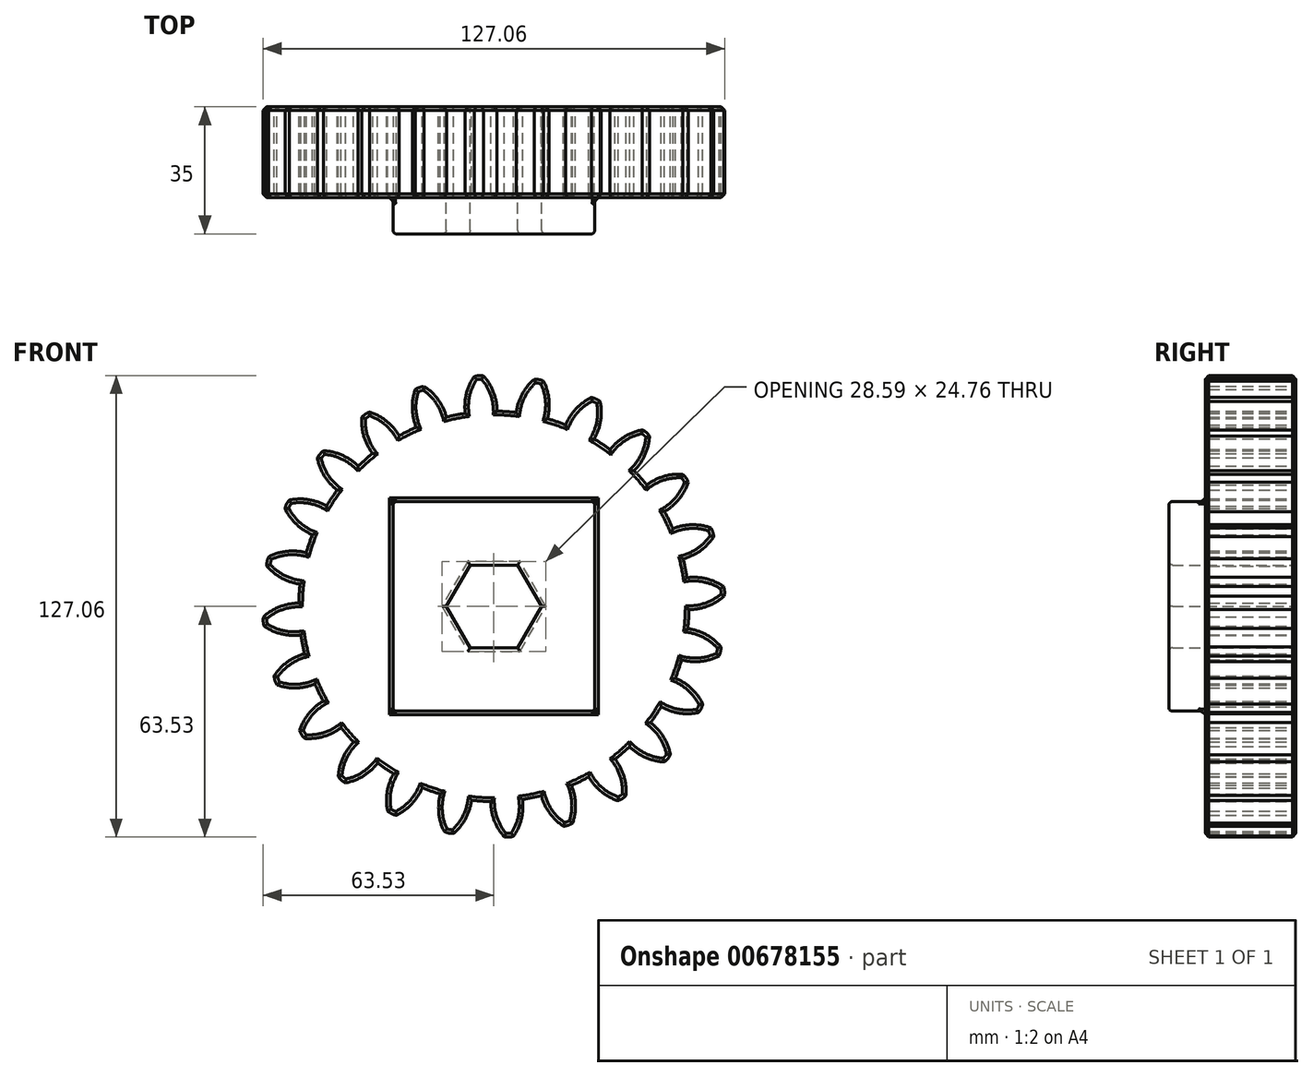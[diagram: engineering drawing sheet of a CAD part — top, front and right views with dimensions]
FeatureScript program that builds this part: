
annotation { "Feature Type Name" : "Feature", "Feature Type Description" : "" }
export const myFeature = defineFeature(function(context is Context, id is Id, definition is map)
    precondition{}
    {
        {
            var Q0;
            Q0=qCreatedBy(makeId("Front.planeOp"),FACE);
            var sketch = newSketch(context, id + "F0", { "sketchPlane" : qUnion([Q0])});
            skCircle(sketch, "E0", {"center": v(0, 0) * mm, "radius": 53.72 * mm});
            skCircle(sketch, "E1", {"center": v(0, 0) * mm, "radius": 58.67 * mm, "construction": true});
            skCircle(sketch, "E2", {"center": v(0, 0) * mm, "radius": 63.5 * mm, "construction": true});
            skLineSegment(sketch, "E3", {"start": v(0, 0) * mm, "end": v(0, 76.94) * mm, "construction": true});
            skLineSegment(sketch, "E4", {"start": v(0, 0) * mm, "end": v(-5.87, 89.51) * mm, "construction": true});
            skLineSegment(sketch, "E5", {"start": v(0, 58.67) * mm, "end": v(-67.61, 58.67) * mm, "construction": true});
            skLineSegment(sketch, "E6", {"start": v(0, 58.67) * mm, "end": v(-66.6, 34.44) * mm, "construction": true});
            skCircle(sketch, "E7", {"center": v(0, 0) * mm, "radius": 55.14 * mm, "construction": true});
            skCircle(sketch, "E8", {"center": v(0, 58.67) * mm, "radius": 14.6 * mm, "construction": true});
            skCircle(sketch, "E9", {"center": v(-13.72, 53.68) * mm, "radius": 14.6 * mm, "construction": true});
            skArc(sketch, "E10", {"start": v(0, 58.67) * mm, "mid": v(-1.2, 61.2) * mm, "end": v(-2.86, 63.44) * mm});
            skArc(sketch, "E11", {"start": v(0.88, 53.71) * mm, "mid": v(0.65, 56.23) * mm, "end": v(0, 58.67) * mm});
            skArc(sketch, "E12.MirrorCS", {"start": v(-7.66, 58.17) * mm, "mid": v(-6.8, 60.83) * mm, "end": v(-5.45, 63.27) * mm});
            skArc(sketch, "E13.MirrorCS", {"start": v(-7.88, 53.14) * mm, "mid": v(-7.98, 55.67) * mm, "end": v(-7.66, 58.17) * mm});
            skArc(sketch, "E14", {"start": v(-2.86, 63.44) * mm, "mid": v(-4.16, 63.52) * mm, "end": v(-5.45, 63.27) * mm});
            skCircle(sketch, "E15.cCircle", {"center": v(0, 0) * mm, "radius": 11.38 * mm, "construction": true});
            skLineSegment(sketch, "E15.0", {"start": v(-6.57, 11.38) * mm, "end": v(6.57, 11.38) * mm});
            skLineSegment(sketch, "E15.1", {"start": v(6.57, 11.38) * mm, "end": v(13.14, 0) * mm});
            skLineSegment(sketch, "E15.2", {"start": v(13.14, 0) * mm, "end": v(6.57, -11.38) * mm});
            skLineSegment(sketch, "E15.3", {"start": v(6.57, -11.38) * mm, "end": v(-6.57, -11.38) * mm});
            skLineSegment(sketch, "E15.4", {"start": v(-6.57, -11.38) * mm, "end": v(-13.14, 0) * mm});
            skLineSegment(sketch, "E15.5", {"start": v(-13.14, 0) * mm, "end": v(-6.57, 11.38) * mm});
            skPoint(sketch, "E15.0.midPoint", {"position": v(0, 11.38) * mm});
            skLineSegment(sketch, "E16.bottom", {"start": v(-27.76, 28.86) * mm, "end": v(27.76, 28.86) * mm});
            skLineSegment(sketch, "E16.top", {"start": v(-27.76, -28.86) * mm, "end": v(27.76, -28.86) * mm});
            skLineSegment(sketch, "E16.left", {"start": v(-27.76, 28.86) * mm, "end": v(-27.76, -28.86) * mm});
            skLineSegment(sketch, "E16.right", {"start": v(27.76, 28.86) * mm, "end": v(27.76, -28.86) * mm});
            skSolve(sketch);
        }
        {
            var Q0;
            {var subQ0=sQuery(id+"F0.wireOp",EDGE,"E0");var subQ1=makeQuery(id+"F0.imprint","INTERSECT",VERTEX,{"derivedFrom":[subQ0,sQuery(id+"F0.wireOp",EDGE,"E11")]});Q0=makeQuery(id+"F0.imprint","IMPRINT",FACE,{"disambiguationData":[TD([[makeQuery(id+"F0.imprint","IMPRINT",EDGE,{"disambiguationData":[TD([[subQ1,-1.0]])],"derivedFrom":subQ0}),1.0]])]});}
            var Q1;
            Q1=makeQuery(id+"F0.imprint","IMPRINT",FACE,{"disambiguationData":[TD([[makeQuery(id+"F0.imprint","IMPRINT",EDGE,{"derivedFrom":sQuery(id+"F0.wireOp",EDGE,"E10")}),1.0]])]});
            extrude(context, id + "F1", {"entities" : qUnion([Q0, Q1]), "depth" : 25 * mm, "offsetDistance" : 25 * mm});
        }
        {
            var Q0;
            Q0=makeQuery(id+"F1.opExtrude","SWEPT_BODY",BODY,{"disambiguationData":[OSD([sQuery(id+"F0.wireOp",EDGE,"E0"),sQuery(id+"F0.wireOp",EDGE,"E10"),sQuery(id+"F0.wireOp",EDGE,"E11"),sQuery(id+"F0.wireOp",EDGE,"E12.MirrorCS"),sQuery(id+"F0.wireOp",EDGE,"E13.MirrorCS"),sQuery(id+"F0.wireOp",EDGE,"E14")])]});
            var Q1;
            Q1=makeQuery(id+"F1.opExtrude","SWEPT_FACE",FACE,{"disambiguationData":[OSD([sQuery(id+"F0.wireOp",EDGE,"E0")])]});
            circularPattern(context, id + "F2", {"entities" : qUnion([Q0]), "axis" : qUnion([Q1]), "angle" : 360 * degree, "instanceCount" : 24, "equalSpace" : true});
        }
        {
            var Q0;
            Q0=makeQuery(id+"F0.imprint","IMPRINT",FACE,{"disambiguationData":[TD([[makeQuery(id+"F0.imprint","IMPRINT",EDGE,{"derivedFrom":sQuery(id+"F0.wireOp",EDGE,"E15.0")}),1.0]])]});
            extrude(context, id + "F3", {"entities" : qUnion([Q0]), "operationType" : NewBodyOperationType.ADD, "depth" : 35 * mm, "offsetDistance" : 25 * mm});
        }
        {
            var Q0;
            {var subQ0=makeQuery(id+"F1.opExtrude","CAP_FACE",FACE,{"disambiguationData":[OSD([sQuery(id+"F0.wireOp",EDGE,"E0"),sQuery(id+"F0.wireOp",EDGE,"E10"),sQuery(id+"F0.wireOp",EDGE,"E11"),sQuery(id+"F0.wireOp",EDGE,"E12.MirrorCS"),sQuery(id+"F0.wireOp",EDGE,"E13.MirrorCS"),sQuery(id+"F0.wireOp",EDGE,"E14"),sQuery(id+"F0.wireOp",EDGE,"E16.bottom"),sQuery(id+"F0.wireOp",EDGE,"E16.top"),sQuery(id+"F0.wireOp",EDGE,"E16.left"),sQuery(id+"F0.wireOp",EDGE,"E16.right")])],"isStart":false});Q0=makeQuery(id+"F3.boolean.opBoolean","MERGE",FACE,{"derivedFrom":[subQ0,makeQuery(id+"F2.opPattern","COPY",FACE,{"derivedFrom":subQ0,"instanceName":"1"}),makeQuery(id+"F2.opPattern","COPY",FACE,{"derivedFrom":subQ0,"instanceName":"2"}),makeQuery(id+"F2.opPattern","COPY",FACE,{"derivedFrom":subQ0,"instanceName":"3"}),makeQuery(id+"F2.opPattern","COPY",FACE,{"derivedFrom":subQ0,"instanceName":"4"}),makeQuery(id+"F2.opPattern","COPY",FACE,{"derivedFrom":subQ0,"instanceName":"5"}),makeQuery(id+"F2.opPattern","COPY",FACE,{"derivedFrom":subQ0,"instanceName":"6"}),makeQuery(id+"F2.opPattern","COPY",FACE,{"derivedFrom":subQ0,"instanceName":"7"}),makeQuery(id+"F2.opPattern","COPY",FACE,{"derivedFrom":subQ0,"instanceName":"8"}),makeQuery(id+"F2.opPattern","COPY",FACE,{"derivedFrom":subQ0,"instanceName":"9"}),makeQuery(id+"F2.opPattern","COPY",FACE,{"derivedFrom":subQ0,"instanceName":"10"}),makeQuery(id+"F2.opPattern","COPY",FACE,{"derivedFrom":subQ0,"instanceName":"11"}),makeQuery(id+"F2.opPattern","COPY",FACE,{"derivedFrom":subQ0,"instanceName":"12"}),makeQuery(id+"F2.opPattern","COPY",FACE,{"derivedFrom":subQ0,"instanceName":"13"}),makeQuery(id+"F2.opPattern","COPY",FACE,{"derivedFrom":subQ0,"instanceName":"14"}),makeQuery(id+"F2.opPattern","COPY",FACE,{"derivedFrom":subQ0,"instanceName":"15"}),makeQuery(id+"F2.opPattern","COPY",FACE,{"derivedFrom":subQ0,"instanceName":"16"}),makeQuery(id+"F2.opPattern","COPY",FACE,{"derivedFrom":subQ0,"instanceName":"17"}),makeQuery(id+"F2.opPattern","COPY",FACE,{"derivedFrom":subQ0,"instanceName":"18"}),makeQuery(id+"F2.opPattern","COPY",FACE,{"derivedFrom":subQ0,"instanceName":"19"}),makeQuery(id+"F2.opPattern","COPY",FACE,{"derivedFrom":subQ0,"instanceName":"20"}),makeQuery(id+"F2.opPattern","COPY",FACE,{"derivedFrom":subQ0,"instanceName":"21"}),makeQuery(id+"F2.opPattern","COPY",FACE,{"derivedFrom":subQ0,"instanceName":"22"}),makeQuery(id+"F2.opPattern","COPY",FACE,{"derivedFrom":subQ0,"instanceName":"23"})]});}
            var Q1;
            {var subQ0=sQuery(id+"F0.wireOp",EDGE,"E16.right");var subQ1=sQuery(id+"F0.wireOp",EDGE,"E16.left");var subQ2=sQuery(id+"F0.wireOp",EDGE,"E16.top");var subQ3=sQuery(id+"F0.wireOp",EDGE,"E16.bottom");var subQ4=makeQuery(id+"F1.opExtrude","CAP_FACE",FACE,{"disambiguationData":[OSD([sQuery(id+"F0.wireOp",EDGE,"E0"),sQuery(id+"F0.wireOp",EDGE,"E10"),sQuery(id+"F0.wireOp",EDGE,"E11"),sQuery(id+"F0.wireOp",EDGE,"E12.MirrorCS"),sQuery(id+"F0.wireOp",EDGE,"E13.MirrorCS"),sQuery(id+"F0.wireOp",EDGE,"E14"),subQ3,subQ2,subQ1,subQ0])],"isStart":true});Q1=makeQuery(id+"F3.boolean.opBoolean","MERGE",FACE,{"derivedFrom":[subQ4,makeQuery(id+"F2.opPattern","COPY",FACE,{"derivedFrom":subQ4,"instanceName":"1"}),makeQuery(id+"F2.opPattern","COPY",FACE,{"derivedFrom":subQ4,"instanceName":"2"}),makeQuery(id+"F2.opPattern","COPY",FACE,{"derivedFrom":subQ4,"instanceName":"3"}),makeQuery(id+"F2.opPattern","COPY",FACE,{"derivedFrom":subQ4,"instanceName":"4"}),makeQuery(id+"F2.opPattern","COPY",FACE,{"derivedFrom":subQ4,"instanceName":"5"}),makeQuery(id+"F2.opPattern","COPY",FACE,{"derivedFrom":subQ4,"instanceName":"6"}),makeQuery(id+"F2.opPattern","COPY",FACE,{"derivedFrom":subQ4,"instanceName":"7"}),makeQuery(id+"F2.opPattern","COPY",FACE,{"derivedFrom":subQ4,"instanceName":"8"}),makeQuery(id+"F2.opPattern","COPY",FACE,{"derivedFrom":subQ4,"instanceName":"9"}),makeQuery(id+"F2.opPattern","COPY",FACE,{"derivedFrom":subQ4,"instanceName":"10"}),makeQuery(id+"F2.opPattern","COPY",FACE,{"derivedFrom":subQ4,"instanceName":"11"}),makeQuery(id+"F2.opPattern","COPY",FACE,{"derivedFrom":subQ4,"instanceName":"12"}),makeQuery(id+"F2.opPattern","COPY",FACE,{"derivedFrom":subQ4,"instanceName":"13"}),makeQuery(id+"F2.opPattern","COPY",FACE,{"derivedFrom":subQ4,"instanceName":"14"}),makeQuery(id+"F2.opPattern","COPY",FACE,{"derivedFrom":subQ4,"instanceName":"15"}),makeQuery(id+"F2.opPattern","COPY",FACE,{"derivedFrom":subQ4,"instanceName":"16"}),makeQuery(id+"F2.opPattern","COPY",FACE,{"derivedFrom":subQ4,"instanceName":"17"}),makeQuery(id+"F2.opPattern","COPY",FACE,{"derivedFrom":subQ4,"instanceName":"18"}),makeQuery(id+"F2.opPattern","COPY",FACE,{"derivedFrom":subQ4,"instanceName":"19"}),makeQuery(id+"F2.opPattern","COPY",FACE,{"derivedFrom":subQ4,"instanceName":"20"}),makeQuery(id+"F2.opPattern","COPY",FACE,{"derivedFrom":subQ4,"instanceName":"21"}),makeQuery(id+"F2.opPattern","COPY",FACE,{"derivedFrom":subQ4,"instanceName":"22"}),makeQuery(id+"F2.opPattern","COPY",FACE,{"derivedFrom":subQ4,"instanceName":"23"}),makeQuery(id+"F3.opExtrude","CAP_FACE",FACE,{"disambiguationData":[OSD([sQuery(id+"F0.wireOp",EDGE,"E15.0"),sQuery(id+"F0.wireOp",EDGE,"E15.1"),sQuery(id+"F0.wireOp",EDGE,"E15.2"),sQuery(id+"F0.wireOp",EDGE,"E15.3"),sQuery(id+"F0.wireOp",EDGE,"E15.4"),sQuery(id+"F0.wireOp",EDGE,"E15.5"),subQ3,subQ2,subQ1,subQ0])],"isStart":true})]});}
            chamfer(context, id + "F4", {"entities" : qUnion([Q0, Q1]), "width" : 1 * mm, "tangentPropagation" : true});
        }
        {
            var Q0;
            Q0=makeQuery(id+"F3.opExtrude","CAP_FACE",FACE,{"disambiguationData":[OSD([sQuery(id+"F0.wireOp",EDGE,"E15.0"),sQuery(id+"F0.wireOp",EDGE,"E15.1"),sQuery(id+"F0.wireOp",EDGE,"E15.2"),sQuery(id+"F0.wireOp",EDGE,"E15.3"),sQuery(id+"F0.wireOp",EDGE,"E15.4"),sQuery(id+"F0.wireOp",EDGE,"E15.5"),sQuery(id+"F0.wireOp",EDGE,"E16.bottom"),sQuery(id+"F0.wireOp",EDGE,"E16.top"),sQuery(id+"F0.wireOp",EDGE,"E16.left"),sQuery(id+"F0.wireOp",EDGE,"E16.right")])],"isStart":false});
            var Q1;
            Q1=makeQuery(id+"F3.opExtrude","SWEPT_FACE",FACE,{"disambiguationData":[OSD([sQuery(id+"F0.wireOp",EDGE,"E16.left")])]});
            var Q2;
            Q2=makeQuery(id+"F3.opExtrude","SWEPT_FACE",FACE,{"disambiguationData":[OSD([sQuery(id+"F0.wireOp",EDGE,"E16.right")])]});
            var Q3;
            Q3=makeQuery(id+"F3.opExtrude","SWEPT_FACE",FACE,{"disambiguationData":[OSD([sQuery(id+"F0.wireOp",EDGE,"E16.bottom")])]});
            var Q4;
            Q4=makeQuery(id+"F3.opExtrude","SWEPT_FACE",FACE,{"disambiguationData":[OSD([sQuery(id+"F0.wireOp",EDGE,"E16.top")])]});
            fillet(context, id + "F5", {"entities" : qUnion([Q0, Q1, Q2, Q3, Q4]), "radius" : 1 * mm, "tangentPropagation" : true, "allowEdgeOverflow" : false});
        }
    });
